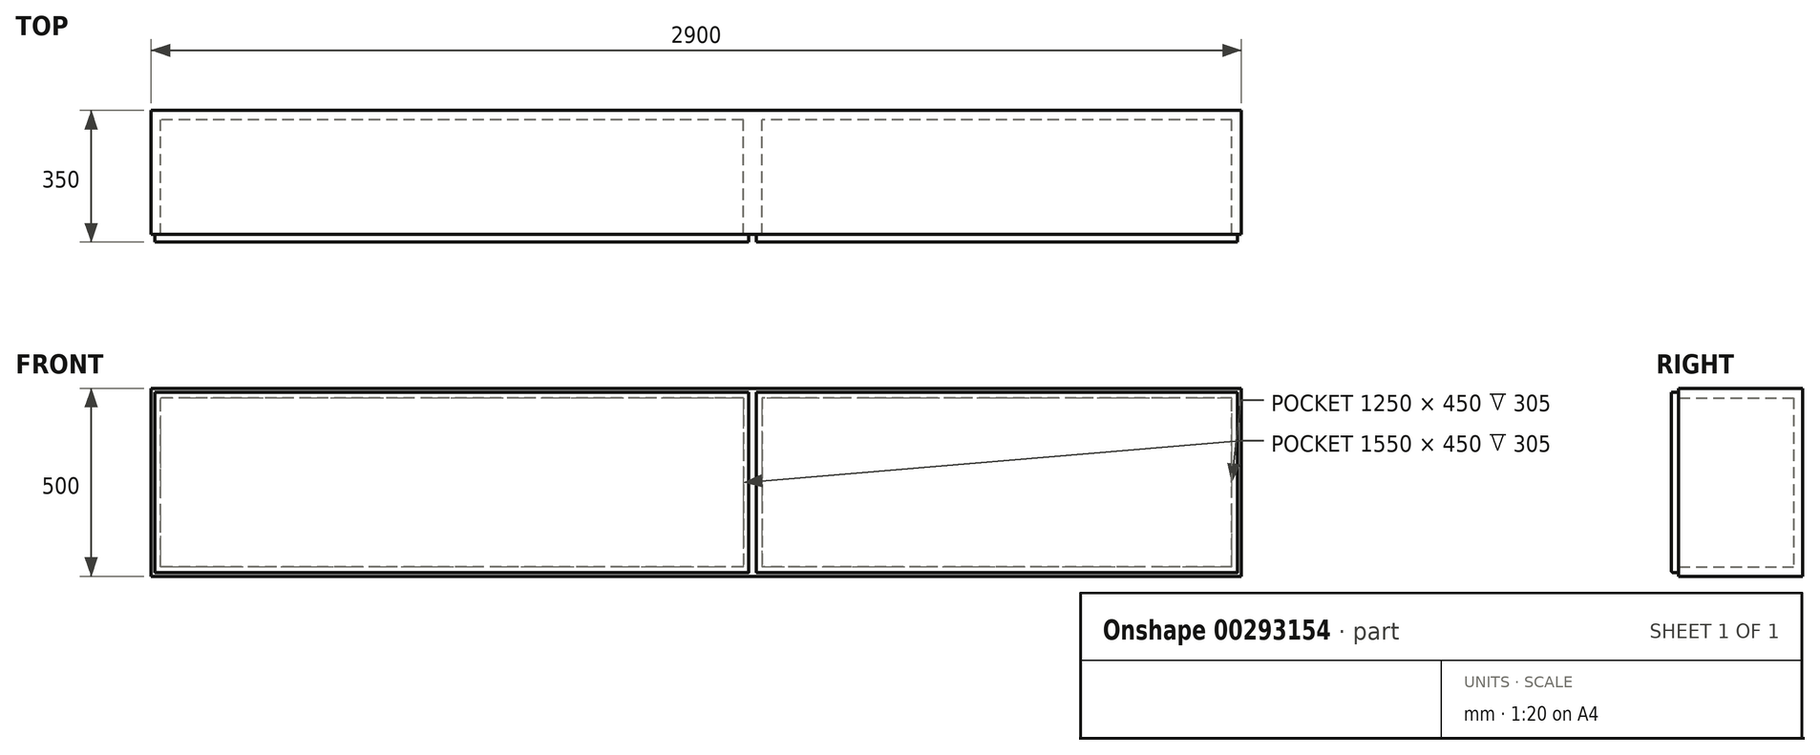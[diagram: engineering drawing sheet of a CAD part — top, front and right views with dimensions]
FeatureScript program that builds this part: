
annotation { "Feature Type Name" : "Feature", "Feature Type Description" : "" }
export const myFeature = defineFeature(function(context is Context, id is Id, definition is map)
    precondition{}
    {
        {
            var Q0;
            Q0=qCreatedBy(makeId("Front.planeOp"),FACE);
            var sketch = newSketch(context, id + "F0", { "sketchPlane" : qUnion([Q0])});
            skLineSegment(sketch, "E0.bottom", {"start": v(1450, 0) * mm, "end": v(-1450, 0) * mm});
            skLineSegment(sketch, "E0.top", {"start": v(1450, 500) * mm, "end": v(-1450, 500) * mm});
            skLineSegment(sketch, "E0.left", {"start": v(1450, 0) * mm, "end": v(1450, 500) * mm});
            skLineSegment(sketch, "E0.right", {"start": v(-1450, 0) * mm, "end": v(-1450, 500) * mm});
            skPoint(sketch, "E0.middle", {"position": v(0, 250) * mm});
            skSolve(sketch);
        }
        {
            var Q0;
            Q0 = qSketchRegion(id + "F0", true);
            extrude(context, id + "F1", {"entities" : qUnion([Q0]), "depth" : 330 * mm});
        }
        {
            var Q0;
            Q0=makeQuery(id+"F1.opExtrude","CAP_FACE",FACE,{"disambiguationData":[OSD([sQuery(id+"F0.wireOp",EDGE,"E0.bottom"),sQuery(id+"F0.wireOp",EDGE,"E0.top"),sQuery(id+"F0.wireOp",EDGE,"E0.left"),sQuery(id+"F0.wireOp",EDGE,"E0.right")])],"isStart":false});
            shell(context, id + "F2", {"entities" : qUnion([Q0]), "thickness" : 25 * mm});
        }
        {
            var Q0;
            Q0=makeQuery(id+"F2.opShell","OFFSET_FACE",FACE,{"disambiguationData":[OSD([sQuery(id+"F0.wireOp",EDGE,"E0.bottom"),sQuery(id+"F0.wireOp",EDGE,"E0.top"),sQuery(id+"F0.wireOp",EDGE,"E0.left"),sQuery(id+"F0.wireOp",EDGE,"E0.right")])]});
            var sketch = newSketch(context, id + "F3", { "sketchPlane" : qUnion([Q0])});
            skLineSegment(sketch, "E1.bottom", {"start": v(125, 475) * mm, "end": v(150, 475) * mm});
            skLineSegment(sketch, "E1.top", {"start": v(125, 25) * mm, "end": v(150, 25) * mm});
            skLineSegment(sketch, "E1.left", {"start": v(125, 475) * mm, "end": v(125, 25) * mm});
            skLineSegment(sketch, "E1.right", {"start": v(150, 475) * mm, "end": v(150, 25) * mm});
            skLineSegment(sketch, "E2.bottom", {"start": v(150, 475) * mm, "end": v(175, 475) * mm});
            skLineSegment(sketch, "E2.top", {"start": v(150, 25) * mm, "end": v(175, 25) * mm});
            skLineSegment(sketch, "E2.right", {"start": v(175, 475) * mm, "end": v(175, 25) * mm});
            skSolve(sketch);
        }
        {
            var Q0;
            Q0 = qSketchRegion(id + "F3", true);
            var Q1;
            Q1=makeQuery(id+"F1.opExtrude","CAP_FACE",FACE,{"disambiguationData":[OSD([sQuery(id+"F0.wireOp",EDGE,"E0.bottom"),sQuery(id+"F0.wireOp",EDGE,"E0.top"),sQuery(id+"F0.wireOp",EDGE,"E0.left"),sQuery(id+"F0.wireOp",EDGE,"E0.right")])],"isStart":false});
            extrude(context, id + "F4", {"entities" : qUnion([Q0]), "operationType" : NewBodyOperationType.ADD, "endBound" : BoundingType.UP_TO_SURFACE, "endBoundEntityFace" : qUnion([Q1]), "depth" : 25 * mm});
        }
        {
            var Q0;
            Q0=makeQuery(id+"F4.boolean.opBoolean","MERGE",FACE,{"derivedFrom":[makeQuery(id+"F1.opExtrude","CAP_FACE",FACE,{"disambiguationData":[OSD([sQuery(id+"F0.wireOp",EDGE,"E0.bottom"),sQuery(id+"F0.wireOp",EDGE,"E0.top"),sQuery(id+"F0.wireOp",EDGE,"E0.left"),sQuery(id+"F0.wireOp",EDGE,"E0.right")])],"isStart":false}),makeQuery(id+"F4.opExtrude","CAP_FACE",FACE,{"disambiguationData":[OSD([sQuery(id+"F3.wireOp",EDGE,"E1.bottom"),sQuery(id+"F3.wireOp",EDGE,"E1.top"),sQuery(id+"F3.wireOp",EDGE,"E1.left"),sQuery(id+"F3.wireOp",EDGE,"E2.bottom"),sQuery(id+"F3.wireOp",EDGE,"E2.top"),sQuery(id+"F3.wireOp",EDGE,"E2.right")])],"isStart":false})]});
            var sketch = newSketch(context, id + "F5", { "sketchPlane" : qUnion([Q0])});
            skLineSegment(sketch, "E3.bottom", {"start": v(-1440, 490) * mm, "end": v(140, 490) * mm});
            skLineSegment(sketch, "E3.top", {"start": v(-1440, 10) * mm, "end": v(140, 10) * mm});
            skLineSegment(sketch, "E3.left", {"start": v(-1440, 490) * mm, "end": v(-1440, 10) * mm});
            skLineSegment(sketch, "E3.right", {"start": v(140, 490) * mm, "end": v(140, 10) * mm});
            skLineSegment(sketch, "E4.bottom", {"start": v(160, 490) * mm, "end": v(1440, 490) * mm});
            skLineSegment(sketch, "E4.top", {"start": v(160, 10) * mm, "end": v(1440, 10) * mm});
            skLineSegment(sketch, "E4.left", {"start": v(160, 490) * mm, "end": v(160, 10) * mm});
            skLineSegment(sketch, "E4.right", {"start": v(1440, 490) * mm, "end": v(1440, 10) * mm});
            skSolve(sketch);
        }
        {
            var Q0;
            Q0 = qSketchRegion(id + "F5", true);
            extrude(context, id + "F6", {"entities" : qUnion([Q0]), "depth" : 20 * mm});
        }
        {
            var Q0;
            Q0=makeQuery(id+"F6.opExtrude","CAP_EDGE",EDGE,{"disambiguationData":[OSD([sQuery(id+"F5.wireOp",EDGE,"E3.top")])],"isStart":false});
            var Q1;
            Q1=makeQuery(id+"F6.opExtrude","CAP_EDGE",EDGE,{"disambiguationData":[OSD([sQuery(id+"F5.wireOp",EDGE,"E4.top")])],"isStart":false});
            fillet(context, id + "F7", {"entities" : qUnion([Q0, Q1]), "radius" : 5 * mm, "tangentPropagation" : true, "allowEdgeOverflow" : false});
        }
    });
